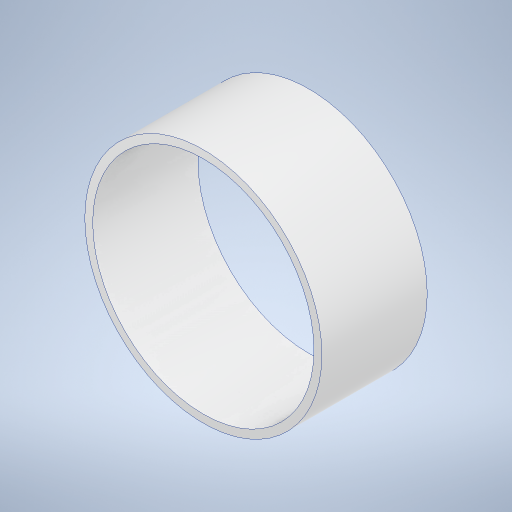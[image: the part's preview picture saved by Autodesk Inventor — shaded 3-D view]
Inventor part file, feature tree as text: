
AUTODESK INVENTOR PART (.ipt)
format: ipt  version: 2024 (Build 280153000, 153)  size: 229,888 bytes
history: native  units: mm
features: extrude x1, sketch x1
ambient origin geometry x8: Origin, YZ Plane, XZ Plane, XY Plane, X Axis, Y Axis, Z Axis, Center Point
bodies: Solid1 (feature_tree)
feature tree (2):
  extrude  "Extrusion1"  Depth=20.0mm
  sketch  "Sketch1"  dims[d0=42.0mm d1=45.0mm d2=20.0mm d3=0.0mm]
